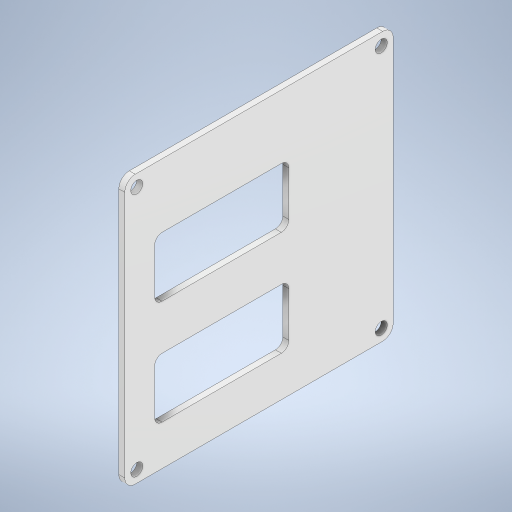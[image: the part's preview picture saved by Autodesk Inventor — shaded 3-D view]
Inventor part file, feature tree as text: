
AUTODESK INVENTOR PART (.ipt)
format: ipt  version: 2024 (Build 280153000, 153)  size: 337,920 bytes
history: native  units: mm
features: extrude x3, sketch x3, fillet x2
ambient origin geometry x8: Origin, YZ Plane, XZ Plane, XY Plane, X Axis, Y Axis, Z Axis, Center Point
bodies: Solid1 (feature_tree)
feature tree (8):
  extrude  "Extrusion1"  Depth=90.0mm
  extrude  "Extrusion2"  Depth=2.0mm
  fillet  "Fillet1"  Radius=4.0mm
  extrude  "Extrusion3"  Depth=2.5mm
  fillet  "Fillet2"  Radius=4.0mm
  sketch  "Sketch1"  dims[d0=90.0mm d1=90.0mm]
  sketch  "Sketch2"  dims[d2=2.0mm d3=0.0mm d4=4.0mm d5=4.0mm]
  sketch  "Sketch3"  dims[d6=4.0mm d7=4.0mm d8=4.0mm d9=4.0mm d10=4.0mm d11=4.0mm d12=4.0mm d13=4.0mm d14=4.0mm d15=4.0mm d16=2.0mm d17=0.0mm d18=3.5mm d19=3.5mm d20=10.0mm d21=20.0mm d22=38.63mm d23=10.0mm d24=20.0mm d25=35.0mm d26=45.0mm d27=20.0mm d28=45.0mm d29=20.0mm d30=10.0mm d31=0.0mm d32=2.5mm]
